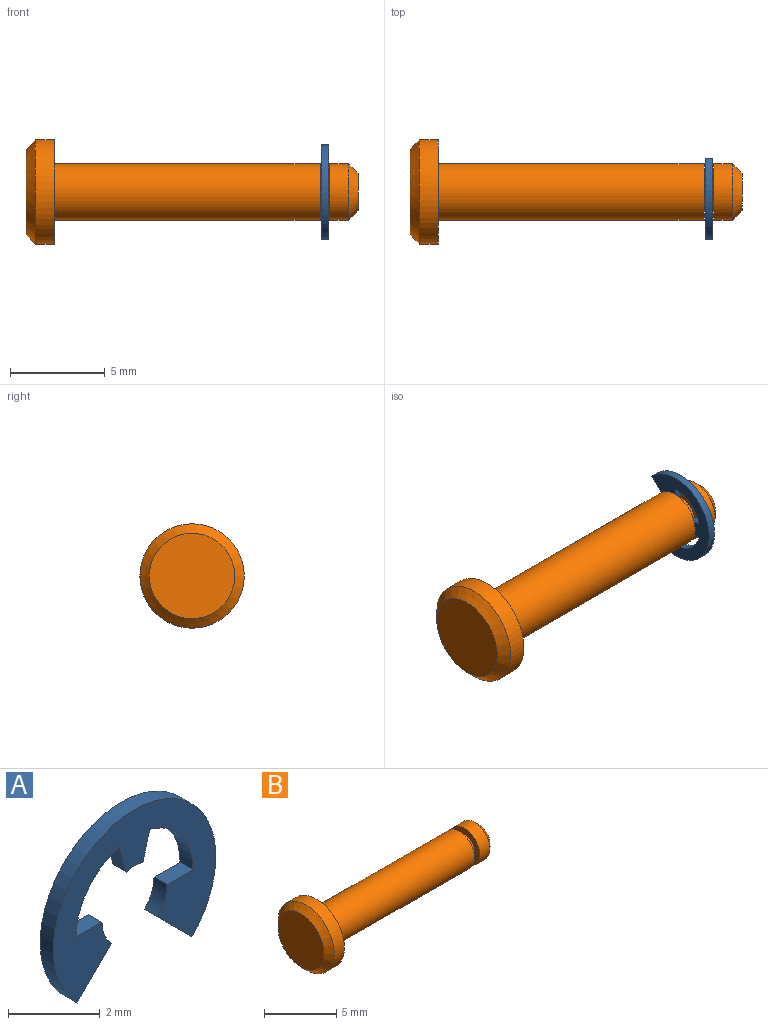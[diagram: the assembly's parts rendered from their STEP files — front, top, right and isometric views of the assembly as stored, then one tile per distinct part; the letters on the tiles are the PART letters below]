
ASSEMBLY  parts=2 mates=1
PART A: 14 faces, bbox 5x0.4x4.3 mm
  f0: plane 1.06x1.06mm, normal (-0.71,0,-0.71), area 0.6mm2, adj f1,f11,f12,f13
  f1: cylinder r=2.5mm len=5mm, axis (0,1,0), area 4.7mm2, adj f0,f2,f12,f13
  f2: plane 1.06x1.06mm, normal (0.71,0,-0.71), area 0.6mm2, adj f1,f3,f12,f13
  f3: cylinder r=1mm len=0.71mm, axis (0,1,0), area 0.3mm2, adj f2,f4,f12,f13
  f4: plane 0.8x0.4mm, normal (0,0,1), area 0.3mm2, adj f3,f5,f12,f13
  f5: cylinder r=1.8mm len=1.74mm, axis (0,1,0), area 0.9mm2, adj f4,f6,f12,f13
  f6: plane 0.77x0.4mm, normal (-0.97,0,-0.26), area 0.3mm2, adj f5,f7,f12,f13
  f7: cylinder r=1mm len=0.52mm, axis (0,1,0), area 0.2mm2, adj f6,f8,f12,f13
  f8: plane 0.77x0.4mm, normal (0.97,0,-0.26), area 0.3mm2, adj f7,f9,f12,f13
  f9: cylinder r=1.8mm len=1.74mm, axis (0,1,0), area 0.9mm2, adj f8,f10,f12,f13
  f10: plane 0.8x0.4mm, normal (0,0,1), area 0.3mm2, adj f9,f11,f12,f13
  f11: cylinder r=1mm len=0.71mm, axis (0,1,0), area 0.3mm2, adj f0,f10,f12,f13
  f12: plane 5x4.27mm, normal (0,-1,0), area 9.4mm2, adj f0,f1,f2,f3,f4,f5,f6,f7
  f13: plane 5x4.27mm, normal (0,1,0), area 9.4mm2, adj f0,f1,f2,f3,f4,f5,f6,f7
PART B: 11 faces, bbox 17.5x5.5x5.5 mm
  f0: plane 4.5x4.5mm, normal (-1,0,0), area 15.9mm2, adj f1
  f1: cone r=2.25mm half-angle=45deg, axis (1,0,0), area 11.1mm2, adj f0,f2
  f2: cylinder r=2.75mm len=5.5mm, axis (1,0,0), area 17.3mm2, adj f1,f3
  f3: plane 5.5x5.5mm, normal (1,0,0), area 16.7mm2, adj f2,f4
  f4: cylinder r=1.5mm len=14mm, axis (1,0,0), area 131.9mm2, adj f3,f5
  f5: plane 3x3mm, normal (1,0,0), area 3.9mm2, adj f4,f6
  f6: cylinder r=1mm len=2mm, axis (1,0,0), area 3.1mm2, adj f5,f7
  f7: plane 3x3mm, normal (-1,0,0), area 3.9mm2, adj f6,f8
  f8: cylinder r=1.5mm len=3mm, axis (1,0,0), area 9.4mm2, adj f7,f9
  f9: cone r=1.5mm half-angle=45deg, axis (-1,0,0), area 5.6mm2, adj f8,f10
  f10: plane 2x2mm, normal (1,0,0), area 3.1mm2, adj f9
PLACE A rot(axis=(0.58,-0.58,0.58),120deg) t=(15.55,0,0)mm
PLACE B at identity
MATE revolute A.f3 <-> B.f1  axis (-1,0,0) through (15.75,0,0)mm
